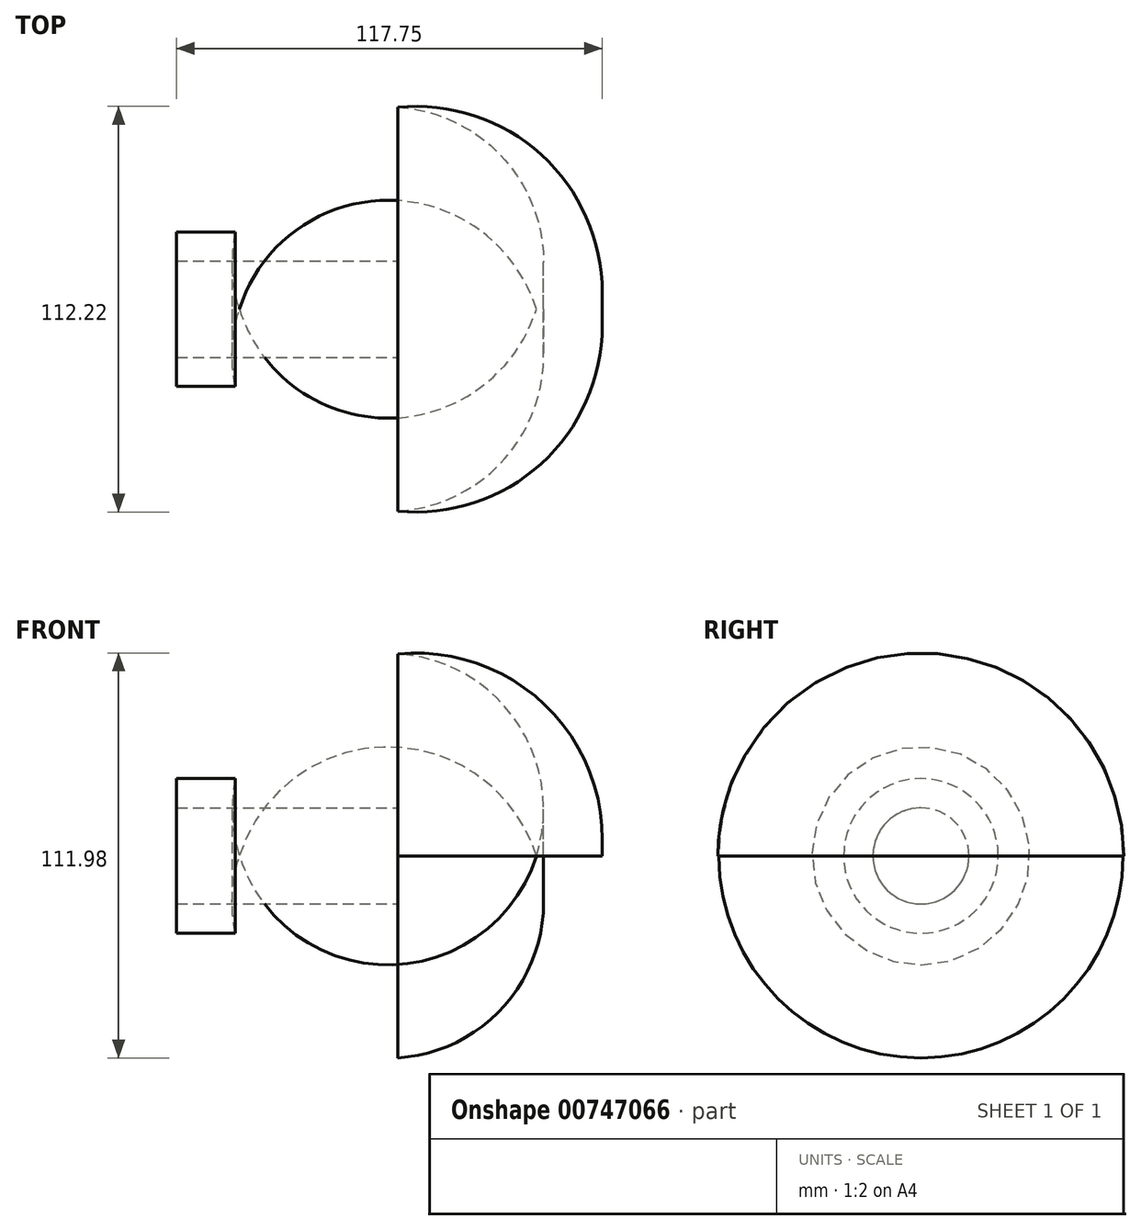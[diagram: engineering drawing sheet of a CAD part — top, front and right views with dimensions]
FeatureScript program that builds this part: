
annotation { "Feature Type Name" : "Feature", "Feature Type Description" : "" }
export const myFeature = defineFeature(function(context is Context, id is Id, definition is map)
    precondition{}
    {
        {
            var Q0;
            Q0=qCreatedBy(makeId("Front.planeOp"),FACE);
            var sketch = newSketch(context, id + "F0", { "sketchPlane" : qUnion([Q0])});
            skLineSegment(sketch, "E0", {"start": v(-44.93, 0) * mm, "end": v(-44.93, 21.38) * mm});
            skArc(sketch, "E1", {"start": v(0, 55.87) * mm, "mid": v(-28.94, 47.06) * mm, "end": v(-44.93, 21.38) * mm});
            skLineSegment(sketch, "E2", {"start": v(-44.93, 0) * mm, "end": v(0, 0) * mm});
            skLineSegment(sketch, "E3", {"start": v(0, 0) * mm, "end": v(0, 55.87) * mm});
            skArc(sketch, "E4", {"start": v(56.36, 0) * mm, "mid": v(41.3, 41.17) * mm, "end": v(0, 55.87) * mm});
            skLineSegment(sketch, "E5", {"start": v(0, 0) * mm, "end": v(56.36, 0) * mm});
            skLineSegment(sketch, "E6", {"start": v(0, 55.87) * mm, "end": v(0, 0) * mm});
            skSolve(sketch);
        }
        {
            var Q0;
            Q0=makeQuery(id+"F0.imprint","IMPRINT",FACE,{"disambiguationData":[TD([[makeQuery(id+"F0.imprint","IMPRINT",EDGE,{"derivedFrom":sQuery(id+"F0.wireOp",EDGE,"E0")}),-1.0]])]});
            var Q1;
            Q1=sQuery(id+"F0.wireOp",EDGE,"E2");
            revolve(context, id + "F1", {"surfaceOperationType" : NewSurfaceOperationType.NEW, "entities" : qUnion([Q0]), "axis" : qUnion([Q1]), "revolveType" : RevolveType.FULL});
        }
        {
            var Q0;
            Q0=makeQuery(id+"F0.imprint","IMPRINT",FACE,{"disambiguationData":[TD([[makeQuery(id+"F0.imprint","IMPRINT",EDGE,{"derivedFrom":sQuery(id+"F0.wireOp",EDGE,"E4")}),1.0]])]});
            var Q1;
            Q1=sQuery(id+"F0.wireOp",EDGE,"E5");
            revolve(context, id + "F2", {"operationType" : NewBodyOperationType.ADD, "surfaceOperationType" : NewSurfaceOperationType.NEW, "entities" : qUnion([Q0]), "axis" : qUnion([Q1]), "revolveType" : RevolveType.SYMMETRIC, "angle" : 180 * degree});
        }
        {
            var Q0;
            Q0=makeQuery(id+"F1.opRevolve","SWEPT_FACE",FACE,{"disambiguationData":[OSD([sQuery(id+"F0.wireOp",EDGE,"E0")])]});
            extrude(context, id + "F3", {"entities" : qUnion([Q0]), "operationType" : NewBodyOperationType.ADD, "depth" : 16.26 * mm, "offsetDistance" : 25.4 * mm});
        }
        {
            var Q0;
            Q0=qCreatedBy(makeId("Right.planeOp"),FACE);
            var sketch = newSketch(context, id + "F4", { "sketchPlane" : qUnion([Q0])});
            skCircle(sketch, "E7", {"center": v(0, 0) * mm, "radius": 13.3 * mm});
            skSolve(sketch);
        }
        {
            var Q0;
            Q0 = qSketchRegion(id + "F4", true);
            extrude(context, id + "F5", {"entities" : qUnion([Q0]), "operationType" : NewBodyOperationType.REMOVE, "oppositeDirection" : true, "depth" : 115.57 * mm, "offsetDistance" : 25.4 * mm});
        }
    });
